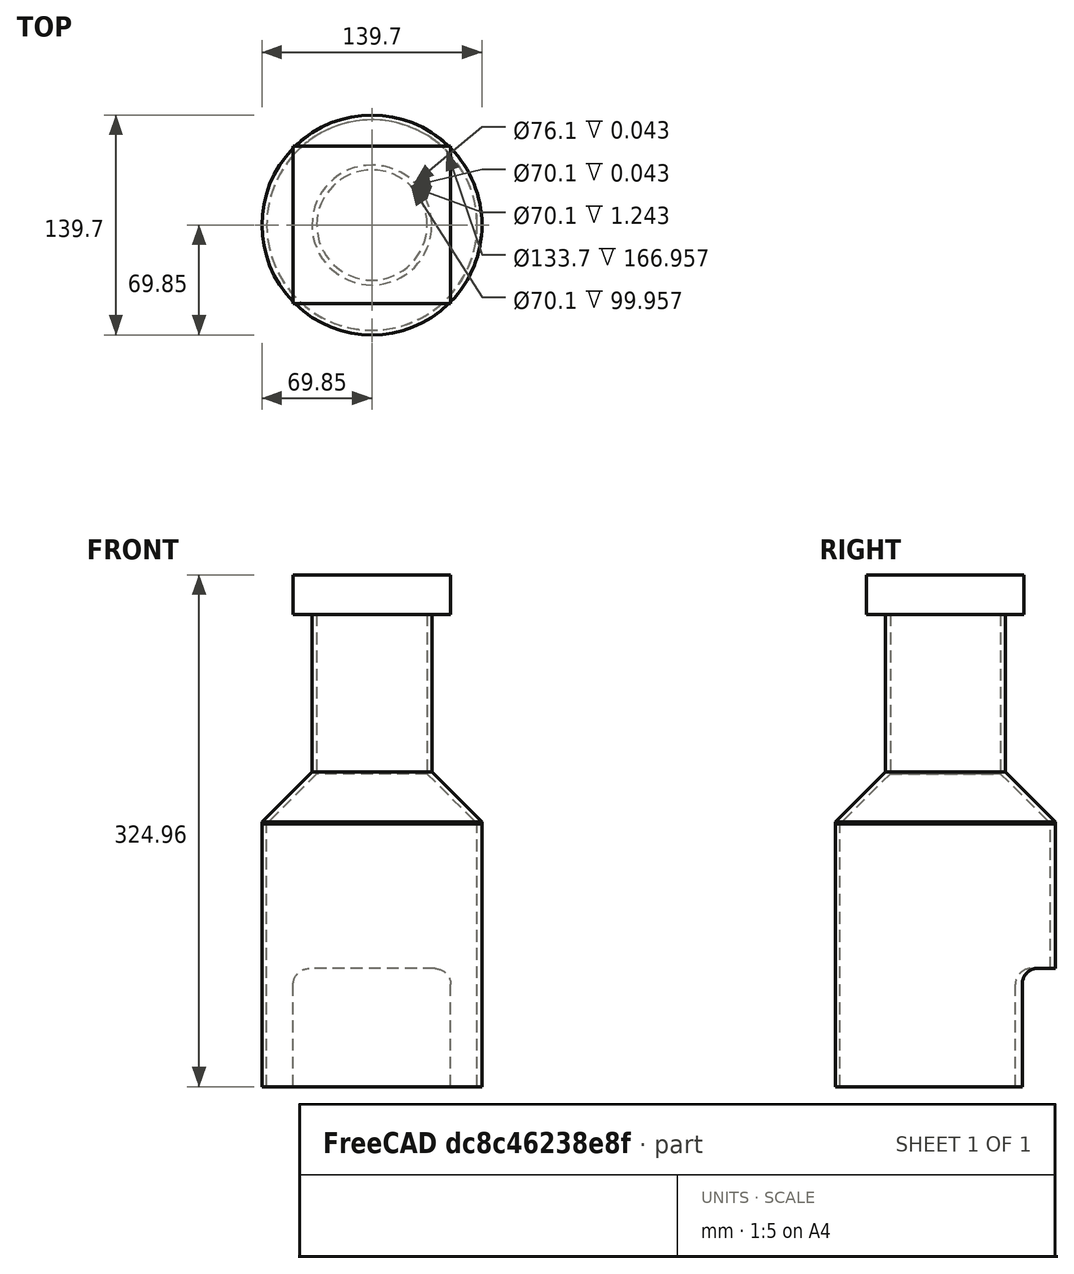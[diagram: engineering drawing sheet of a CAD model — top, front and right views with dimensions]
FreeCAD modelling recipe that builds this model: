
FCSTD DOCUMENT  (FreeCAD 0.21R33694 (Git))
Label: transition3
License: All rights reserved
LicenseURL: http://en.wikipedia.org/wiki/All_rights_reserved
objects: Sketcher::SketchObject×4, Fem::ConstraintForce×4, Part::Revolution×3, Part::FeaturePython×2, Part::Extrusion×1, Part::Cut×1, Part::Box×1, Fem::ConstraintFixed×1, App::MaterialObjectPython×1, Fem::FemSolverObjectPython×1, Fem::FeaturePython×1, Fem::FemMeshObjectPython×1, Fem::FemAnalysis×1
note: 12 computed .brp shape members not serialized (recipe doc carries the construction recipe); baked Part::Feature solids carry a one-line shape summary decoded from their .brp

FEATURE [Sketcher::SketchObject] Sketch
  FullyConstrained = true
  Placement = pos=(0,0,0) rot=(1,0,0;1.5708rad)
  sketch-geometry (6):
    g0: LineSegment StartX=66.85 StartY=0 StartZ=0 EndX=69.85 EndY=0 EndZ=0
    g1: LineSegment StartX=35.05 StartY=33.0426 StartZ=0 EndX=38.05 EndY=33.0426 EndZ=0
    g2: LineSegment StartX=35.05 StartY=33.0426 StartZ=0 EndX=35.05 EndY=31.8 EndZ=0
    g3: LineSegment StartX=69.85 StartY=0 StartZ=0 EndX=69.85 EndY=1.24264 EndZ=0
    g4: LineSegment StartX=35.05 StartY=31.8 StartZ=0 EndX=66.85 EndY=0 EndZ=0
    g5: LineSegment StartX=38.05 StartY=33.0426 StartZ=0 EndX=69.85 EndY=1.24264 EndZ=0
  constraints (18):
    c: PointOnObject(g0,g-1)
    c: DistanceX(g-1,g1) = 35.05
    c: DistanceX(g-1,g0) = 66.85
    c: DistanceX(g0,g0) = 3
    c: Horizontal(g0)
    c: Horizontal(g1)
    c: DistanceX(g1,g1) = 3
    c: Coincident(g2,g1)
    c: Vertical(g2)
    c: Coincident(g3,g0)
    c: Vertical(g3)
    c: Coincident(g4,g2)
    c: Coincident(g4,g0)
    c: Coincident(g5,g1)
    c: Coincident(g5,g3)
    c: Angle(g4,g-1) = 0.785398
    c: DistanceY(g2,g2) = 1.24264
    c: DistanceY(g3,g3) = 1.24264
FEATURE [Sketcher::SketchObject] Sketch001
  ExternalGeometry = -> [Sketch]
  FullyConstrained = true
  Placement = pos=(0,0,0) rot=(1,0,0;1.5708rad)
  sketch-geometry (4):
    g0: LineSegment StartX=35.05 StartY=33.0426 StartZ=0 EndX=38.05 EndY=33.0426 EndZ=0
    g1: LineSegment StartX=38.05 StartY=33.0426 StartZ=0 EndX=38.05 EndY=133.043 EndZ=0
    g2: LineSegment StartX=38.05 StartY=133.043 StartZ=0 EndX=35.05 EndY=133.043 EndZ=0
    g3: LineSegment StartX=35.05 StartY=133.043 StartZ=0 EndX=35.05 EndY=33.0426 EndZ=0
  constraints (11):
    c: Coincident(g0,g1)
    c: Coincident(g1,g2)
    c: Coincident(g2,g3)
    c: Coincident(g3,g0)
    c: Horizontal(g0)
    c: Horizontal(g2)
    c: Vertical(g1)
    c: Vertical(g3)
    c: Coincident(g0,g-3)
    c: DistanceY(g1,g1) = 100
    c: DistanceX(g0,g0) = 3
FEATURE [Sketcher::SketchObject] Sketch002
  ExternalGeometry = -> [Sketch]
  FullyConstrained = true
  Placement = pos=(0,0,0) rot=(1,0,0;1.5708rad)
  sketch-geometry (4):
    g0: LineSegment StartX=66.85 StartY=0 StartZ=0 EndX=69.85 EndY=0 EndZ=0
    g1: LineSegment StartX=69.85 StartY=0 StartZ=0 EndX=69.85 EndY=-166.957 EndZ=0
    g2: LineSegment StartX=69.85 StartY=-166.957 StartZ=0 EndX=66.85 EndY=-166.957 EndZ=0
    g3: LineSegment StartX=66.85 StartY=-166.957 StartZ=0 EndX=66.85 EndY=0 EndZ=0
  constraints (11):
    c: Coincident(g0,g1)
    c: Coincident(g1,g2)
    c: Coincident(g2,g3)
    c: Coincident(g3,g0)
    c: Horizontal(g0)
    c: Horizontal(g2)
    c: Vertical(g1)
    c: Vertical(g3)
    c: Coincident(g0,g-3)
    c: DistanceX(g0,g0) = 3
    c: DistanceY(g1,g-4) = 200
FEATURE [Part::Revolution] Revolve
  Angle = 360
  Axis = (0,0,1)
  Base = (0,0,0)
  FaceMakerClass = Part::FaceMakerBullseye
  Solid = true
  Source = -> Sketch
  Symmetric = false
FEATURE [Part::Revolution] Revolve001
  Angle = 360
  Axis = (0,0,1)
  Base = (0,0,0)
  FaceMakerClass = Part::FaceMakerBullseye
  Solid = true
  Source = -> Sketch001
  Symmetric = false
FEATURE [Part::Revolution] Revolve002
  Angle = 360
  Axis = (0,0,1)
  Base = (0,0,0)
  FaceMakerClass = Part::FaceMakerBullseye
  Solid = true
  Source = -> Sketch002
  Symmetric = false
FEATURE [Part::FeaturePython] BooleanFragments  # WARN: FeaturePython — macro-defined, semantics opaque (R4)
  Mode = 2
  Objects = -> [Revolve,Revolve001,Revolve002]
  Tolerance = 0
FEATURE [Sketcher::SketchObject] Sketch003
  ExternalGeometry = -> [Sketch]
  FullyConstrained = true
  Placement = pos=(0,70,0) rot=(0,0.707107,0.707107;3.14159rad)
  sketch-geometry (8):
    g0: LineSegment StartX=-40 StartY=-91.9574 StartZ=0 EndX=40 EndY=-91.9574 EndZ=0
    g1: LineSegment StartX=50 StartY=-101.957 StartZ=0 EndX=50 EndY=-581.957 EndZ=0
    g2: LineSegment StartX=40 StartY=-591.957 StartZ=0 EndX=-40 EndY=-591.957 EndZ=0
    g3: LineSegment StartX=-50 StartY=-581.957 StartZ=0 EndX=-50 EndY=-101.957 EndZ=0
    g4: ArcOfCircle CenterX=-40 CenterY=-101.957 CenterZ=0 NormalX=0 NormalY=0 NormalZ=1 AngleXU=0 Radius=10 StartAngle=1.5708 EndAngle=3.14159
    g5: ArcOfCircle CenterX=40 CenterY=-101.957 CenterZ=0 NormalX=0 NormalY=0 NormalZ=1 AngleXU=0 Radius=10 StartAngle=2e-16 EndAngle=1.5708
    g6: ArcOfCircle CenterX=-40 CenterY=-581.957 CenterZ=0 NormalX=0 NormalY=0 NormalZ=1 AngleXU=0 Radius=10 StartAngle=3.14159 EndAngle=4.71239
    g7: ArcOfCircle CenterX=40 CenterY=-581.957 CenterZ=0 NormalX=0 NormalY=0 NormalZ=1 AngleXU=0 Radius=10 StartAngle=4.71239 EndAngle=6.28319
  constraints (20):
    c: Horizontal(g0)
    c: Horizontal(g2)
    c: Vertical(g1)
    c: Vertical(g3)
    c: Tangent(g3,g4) = 1.5708
    c: Tangent(g0,g4) = 1.5708
    c: Tangent(g0,g5) = 1.5708
    c: Tangent(g1,g5) = 1.5708
    c: Tangent(g3,g6) = 1.5708
    c: Tangent(g2,g6) = 1.5708
    c: Tangent(g2,g7) = 1.5708
    c: Tangent(g1,g7) = 1.5708
    c: Radius(g4) = 10
    c: Radius(g5) = 10
    c: Radius(g6) = 10
    c: Radius(g7) = 10
    c: DistanceX(g3,g1) = 100
    c: DistanceY(g2,g0) = 500
    c: DistanceY(g0,g-3) = 125
    c: DistanceX(g-1,g1) = 50
FEATURE [Part::Extrusion] Extrude
  Base = -> Sketch003
  Dir = (0,1,-2e-16)
  DirMode = 2
  FaceMakerClass = Part::FaceMakerBullseye
  LengthFwd = 0
  LengthRev = 50
  Solid = true
  Symmetric = false
FEATURE [Part::Cut] Cut
  Base = -> BooleanFragments
  Tool = -> Extrude
FEATURE [Part::Box] Box  label="Cube"
  AttacherType = Attacher::AttachEngine3D
  Height = 25
  Length = 100
  Placement = pos=(-50,-50,133) rot=(0,0,1;0rad)
  Width = 100
FEATURE [Part::FeaturePython] BooleanFragments001  # WARN: FeaturePython — macro-defined, semantics opaque (R4)
  Mode = 2
  Objects = -> [Cut,Box]
  Tolerance = 0
FEATURE [Fem::ConstraintFixed] ConstraintFixed
  NormalDirection = (0,0,-1)
  References = -> [BooleanFragments001]
  Scale = 11
FEATURE [Fem::ConstraintForce] ConstraintForce  label="my_a"
  Direction = -> BooleanFragments001 [Edge3]
  DirectionVector = (0,0,-1)
  Force = 0.01
  NormalDirection = (-1,0,0)
  Points = (16) [(-50,50,133),(-50,50,141.333),(-50,50,149.667),(-50,50,158),(-50,16.6667,133),(-50,16.6667,141.333),(-50,16.6667,149.667),(-50,16.6667,158),+8 more]
  References = -> [BooleanFragments001]
  Reversed = true
FEATURE [Fem::ConstraintForce] ConstraintForce001  label="my_b"
  Direction = -> BooleanFragments001 [Edge11]
  DirectionVector = (0,0,1)
  Force = 0.01
  NormalDirection = (1,0,0)
  Points = (16) [(50,50,133),(50,50,141.333),(50,50,149.667),(50,50,158),(50,16.6667,133),(50,16.6667,141.333),(50,16.6667,149.667),(50,16.6667,158),(50,-16.6667,133),+7 more]
  References = -> [BooleanFragments001]
FEATURE [Fem::ConstraintForce] ConstraintForce002  label="mx_a"
  Direction = -> BooleanFragments001 [Edge11]
  DirectionVector = (0,0,-1)
  Force = 1000
  NormalDirection = (0,1,0)
  Points = (16) [(-50,50,133),(-50,50,141.333),(-50,50,149.667),(-50,50,158),(-16.6667,50,133),(-16.6667,50,141.333),(-16.6667,50,149.667),(-16.6667,50,158),+8 more]
  References = -> [BooleanFragments001]
  Reversed = true
FEATURE [Fem::ConstraintForce] ConstraintForce003  label="mx_b"
  Direction = -> BooleanFragments001 [Edge6]
  DirectionVector = (0,0,1)
  Force = 1000
  NormalDirection = (0,-1,0)
  Points = (16) [(-50,-50,133),(-50,-50,141.333),(-50,-50,149.667),(-50,-50,158),(-16.6667,-50,133),(-16.6667,-50,141.333),(-16.6667,-50,149.667),(-16.6667,-50,158),+8 more]
  References = -> [BooleanFragments001]
FEATURE [App::MaterialObjectPython] MaterialSolid  # material (typed FeaturePython)
  Category = 0
  Material = AuthorAndLicense=(c) 2014 M. Münch - GNU Lesser General Public License (LGPL),CardName=Steel-St-E-315,Density=7800 kg/m^3,Father=Metal,+13 more (map truncated)
FEATURE [Fem::FemSolverObjectPython] SolverCcxTools  # FEM object (typed FeaturePython)
  AnalysisType = 0
  BeamShellResultOutput3D = false
  BucklingFactors = 1
  EigenmodeHighLimit = 1000000
  EigenmodeLowLimit = 0
  EigenmodesCount = 10
  GeometricalNonlinearity = 0
  IterationsControlParameterCutb = 0.25,0.5,0.75,0.85,,,1.5,
  IterationsControlParameterIter = 4,8,9,200,10,400,,200,,
  IterationsControlParameterTimeUse = false
  IterationsThermoMechMaximum = 2000
  IterationsUserDefinedIncrementations = false
  IterationsUserDefinedTimeStepLength = false
  MaterialNonlinearity = 0
  MatrixSolverType = 0
  SplitInputWriter = false
  ThermoMechSteadyState = true
  TimeEnd = 1
  TimeInitialStep = 0.01
FEATURE [Fem::FeaturePython] MeshRegion  # FEM object (typed FeaturePython)
  CharacteristicLength = 5
  References = -> [BooleanFragments001]
FEATURE [Fem::FemMeshObjectPython] FEMMeshGmsh001  label="FEMMeshGmsh"  # FEM object (typed FeaturePython)
  Algorithm2D = 0
  Algorithm3D = 0
  CharacteristicLengthMax = 30
  CharacteristicLengthMin = 0
  CoherenceMesh = true
  ElementDimension = 0
  ElementOrder = 1
  GeometryTolerance = 1e-06
  GroupsOfNodes = false
  HighOrderOptimize = 0
  MeshRegionList = -> [MeshRegion]
  MeshSizeFromCurvature = 12
  OptimizeNetgen = false
  OptimizeStd = true
  Part = -> BooleanFragments001
  RecombinationAlgorithm = 0
  Recombine3DAll = false
  RecombineAll = false
  SecondOrderLinear = false
FEATURE [Fem::FemAnalysis] Analysis
  Group = -> [ConstraintFixed,ConstraintForce,ConstraintForce001,ConstraintForce002,ConstraintForce003,FEMMeshGmsh001,MaterialSolid,SolverCcxTools]
